# Revit family: STH8103_27
name_source: partatom
category: Luminárias
units: mm (PartAtom-declared; Revit-internal decimal feet)

## family parameters
Com base no plano de trabalho = Não
Compartilhado = Não
Corte com vazios quando carregada = Não
Cota do conector redondo = Utilizar diâmetro
Fonte luminosa = Sim
Manter orientação da anotação = Não
Ponto de cálculo do ambiente = Não
Sempre na vertical = Sim
Tipo de parte = Normal

## types (1)
- STH8103/27 - 12Vcc - 2700K - 150lm - 300°
    Altura = 0.04 m
    Arquivo de rede fotométrica = STELLA - STH8103-27 - BIPINO G4 2W.ies
    Comprimento = 0.02 m
    Cromado = Cromado
    Dimerização = Não dimerizável
    Elevação padrão = 0 m
    Estrutura = Luminoso - 2700K
    Fabricante = Stella
    Filtro de cor = 16777215
    Fluxo Luminoso = 150 lm
    Grau de proteção (IP) = IP20
    IRC (Índice de reprodução de cores) = >80
    Largura = 0.01 m
    Modelo = Bipino G4
    Potência = 2 W
    Referência = STH8103/27 - 12Vcc
    Temperatura da cor (K) = 2700 K
    Tensão Elétrica = 12Vcc
    Troca de temperatura da cor de lâmpada com esmaecimento = <Nenhum>
    URL = https://stella.com.br
    Ângulo de Abertura = 300°
    Ângulo de inclinação = 90.00°
